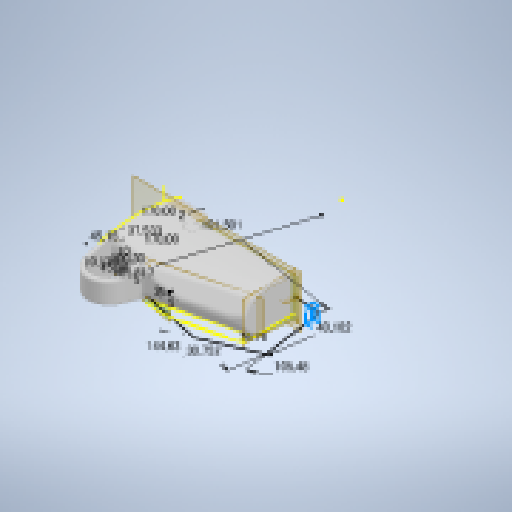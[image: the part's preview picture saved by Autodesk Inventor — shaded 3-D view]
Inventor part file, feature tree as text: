
AUTODESK INVENTOR PART (.ipt)
format: ipt  version: 2025.2 (Build 292293000, 293)  size: 3,676,160 bytes
history: native  units: in
note: dims shown in document units (in); Inventor stores cm internally (conversion verified against a paired STEP export)
features: extrude x39, sketch x34, fillet x32, other x28, reference x28, chamfer x10, projected_geometry x5, mirror x3
ambient origin geometry x8: Origin, YZ Plane, XZ Plane, XY Plane, X Axis, Y Axis, Z Axis, Center Point
bodies: Body1 (feature_tree)
feature tree (179):
  other  "ソリッド1"
  sketch  "スケッチ1"
  extrude  "押し出し1"  Depth=3.3465in
  sketch  "スケッチ4"
  extrude  "押し出し4"  Depth=0.2756in
  extrude  "押し出し5"  Depth=9.8425in
  extrude  "押し出し6"  Depth=0.8661in TaperAngle=0.0deg
  extrude  "押し出し7"  Depth=0.8268in
  chamfer  "面取り1"  Distance=0.1181in
  chamfer  "面取り2"  Distance=0.1181in
  chamfer  "面取り3"  Distance=1.8504in
  chamfer  "面取り4"  Distance=1.1024in
  other  "作業平面3"
  other  "作業平面5"
  extrude  "押し出し8"  Depth=1.5354in
  other  "作業平面6"
  mirror  "ミラー1"
  chamfer  "面取り5"  Distance=3.3465in
  extrude  "押し出し9"  Depth=3.3465in TaperAngle=0.0deg
  fillet  "フィレット27"  Radius=3.3465in
  fillet  "フィレット28"  Radius=3.3465in
  fillet  "フィレット29"  Radius=0.1181in
  fillet  "フィレット30"  Radius=0.1181in
  fillet  "フィレット32"  Radius=0.1181in
  fillet  "フィレット35"  Radius=0.1181in
  fillet  "フィレット36"  Radius=0.3937in
  fillet  "フィレット37"  Radius=0.1575in
  fillet  "フィレット38"  Radius=0.7087in
  fillet  "フィレット42"  [1 undecoded]
  fillet  "フィレット43"  Radius=0.3543in
  fillet  "フィレット44"  Radius=1.9685in
  fillet  "フィレット45"  Radius=2.0866in
  other  "作業平面7"
  extrude  "押し出し10"  Depth=0.1969in
  fillet  "フィレット46"  Radius=0.1969in
  other  "作業平面8"
  extrude  "押し出し11"  Depth=0.7874in
  sketch  "スケッチ10"
  extrude  "押し出し12"  Depth=0.0787in
  extrude  "押し出し13"  Depth=0.3937in
  chamfer  "面取り6"  Distance=0.1181in
  sketch  "スケッチ11"
  chamfer  "面取り7"  Distance=0.1181in
  extrude  "押し出し14"  Depth=0.0354in
  chamfer  "面取り8"  Distance=0.0394in
  chamfer  "面取り9"  Distance=0.0787in
  extrude  "押し出し15"  Depth=0.0118in
  chamfer  "面取り10"  Distance=0.0354in
  other  "作業平面9"
  other  "作業平面10"
  extrude  "押し出し16"  [1 undecoded]
  fillet  "フィレット47"  Radius=0.0394in
  fillet  "フィレット48"  Radius=0.0394in
  fillet  "フィレット49"  Radius=0.0394in
  mirror  "ミラー7"
  mirror  "ミラー8"
  fillet  "フィレット58"  Radius=0.8268in
  fillet  "フィレット59"  Radius=0.0787in
  fillet  "フィレット60"  Radius=0.8268in
  fillet  "フィレット61"  Radius=1.1681in
  fillet  "フィレット62"  Radius=1.1681in
  fillet  "フィレット63"  Radius=0.6299in
  other  "作業平面11"
  extrude  "押し出し17"  TaperAngle=45.0deg  [1 undecoded]
  extrude  "押し出し18"  Depth=0.3937in
  extrude  "押し出し19"  Depth=1.1811in TaperAngle=0.0deg
  extrude  "押し出し20"  Depth=0.3543in TaperAngle=45.0deg
  other  "作業平面13"
  extrude  "押し出し21"  Depth=0.0787in
  fillet  "フィレット66"  Radius=0.1181in
  fillet  "フィレット67"  Radius=0.0709in
  extrude  "押し出し22"  Depth=0.0394in TaperAngle=45.0deg
  other  "作業平面14"
  extrude  "押し出し23"  Depth=0.0394in TaperAngle=45.0deg
  other  "作業平面15"
  extrude  "押し出し24"  Depth=0.0591in TaperAngle=0.0deg
  extrude  "押し出し25"  Depth=0.1969in TaperAngle=45.0deg
  other  "作業平面16"
  extrude  "押し出し26"  Depth=0.0591in TaperAngle=0.0deg
  extrude  "押し出し27"  Depth=3.937in
  other  "作業平面17"
  extrude  "押し出し28"  Depth=1.9685in
  extrude  "押し出し29"  Depth=0.1181in
  other  "作業平面18"
  extrude  "押し出し34"  Depth=0.1181in
  extrude  "押し出し35"  Depth=0.0787in
  fillet  "フィレット68"  Radius=0.0197in
  fillet  "フィレット69"  Radius=0.0197in
  fillet  "フィレット70"  Radius=0.3937in
  extrude  "押し出し36"  Depth=0.1181in
  other  "作業平面19"
  fillet  "フィレット74"  [1 undecoded]
  fillet  "フィレット75"  Radius=1.1811in
  fillet  "フィレット76"  Radius=0.0787in
  sketch  "スケッチ33"
  extrude  "押し出し39"  Depth=0.1181in TaperAngle=0.0deg
  extrude  "押し出し40"  Depth=0.0197in
  other  "作業平面21"
  sketch  "スケッチ37"
  other  "作業平面23"
  other  "作業平面24"
  sketch  "スケッチ39"
  extrude  "押し出し48"  Depth=0.0787in TaperAngle=0.0deg
  extrude  "押し出し49"  Depth=0.9949in TaperAngle=0.0deg
  sketch  "スケッチ42"
  extrude  "押し出し51"  Depth=0.3937in TaperAngle=0.0deg
  extrude  "押し出し53"  Depth=0.0472in
  extrude  "押し出し54"  Depth=0.0669in
  extrude  "押し出し55"  Depth=0.1181in
  fillet  "フィレット77"  Radius=0.3543in
  extrude  "押し出し56"  Depth=0.1181in
  projected_geometry  "投影ループ2"
  sketch  "スケッチ5"
  projected_geometry  "投影ループ3"
  sketch  "スケッチ6"
  projected_geometry  "投影ループ4"
  other  "作業平面2"
  other  "作業平面4"
  sketch  "スケッチ7"
  sketch  "スケッチ8"
  projected_geometry  "投影ループ5"
  sketch  "スケッチ9"
  sketch  "スケッチ12"
  sketch  "スケッチ13"
  sketch  "スケッチ14"
  sketch  "スケッチ15"
  sketch  "スケッチ16"
  sketch  "スケッチ18"
  sketch  "スケッチ19"
  sketch  "スケッチ20"
  sketch  "スケッチ21"
  reference  "参照1"
  reference  "参照2"
  reference  "参照3"
  reference  "参照4"
  reference  "参照5"
  sketch  "スケッチ22"
  reference  "参照6"
  reference  "参照7"
  sketch  "スケッチ23"
  reference  "参照8"
  reference  "参照9"
  reference  "参照10"
  reference  "参照11"
  reference  "参照12"
  reference  "参照13"
  sketch  "スケッチ24"
  projected_geometry  "投影ループ6"
  sketch  "スケッチ25"
  sketch  "スケッチ26"
  sketch  "スケッチ27"
  sketch  "スケッチ28"
  reference  "参照14"
  reference  "参照15"
  sketch  "スケッチ30"
  reference  "参照16"
  sketch  "スケッチ31"
  reference  "参照17"
  reference  "参照18"
  reference  "参照19"
  reference  "参照21"
  reference  "参照22"
  reference  "参照23"
  reference  "参照24"
  reference  "参照25"
  reference  "参照29"
  sketch  "スケッチ32"
  sketch  "スケッチ40"
  reference  "参照31"
  sketch  "スケッチ41"
  reference  "参照32"
  reference  "参照33"
  other  "<userpath>\OneDrive\ドキュメント\New Controller\Hardware\Assembly.iam"
  other  "Assembly.iam"
  other  "Nano33BLE:1"
  other  "Cuicuit:1"
  other  "switch:1"
  other  "mini vibrator:1"
  other  "Body_compleat02:1"
note: 4 required parameter values undecoded (feature->parameter linkage not recoverable at this tier; creation-order binding heuristic only, values carry confidence <= 0.55)
